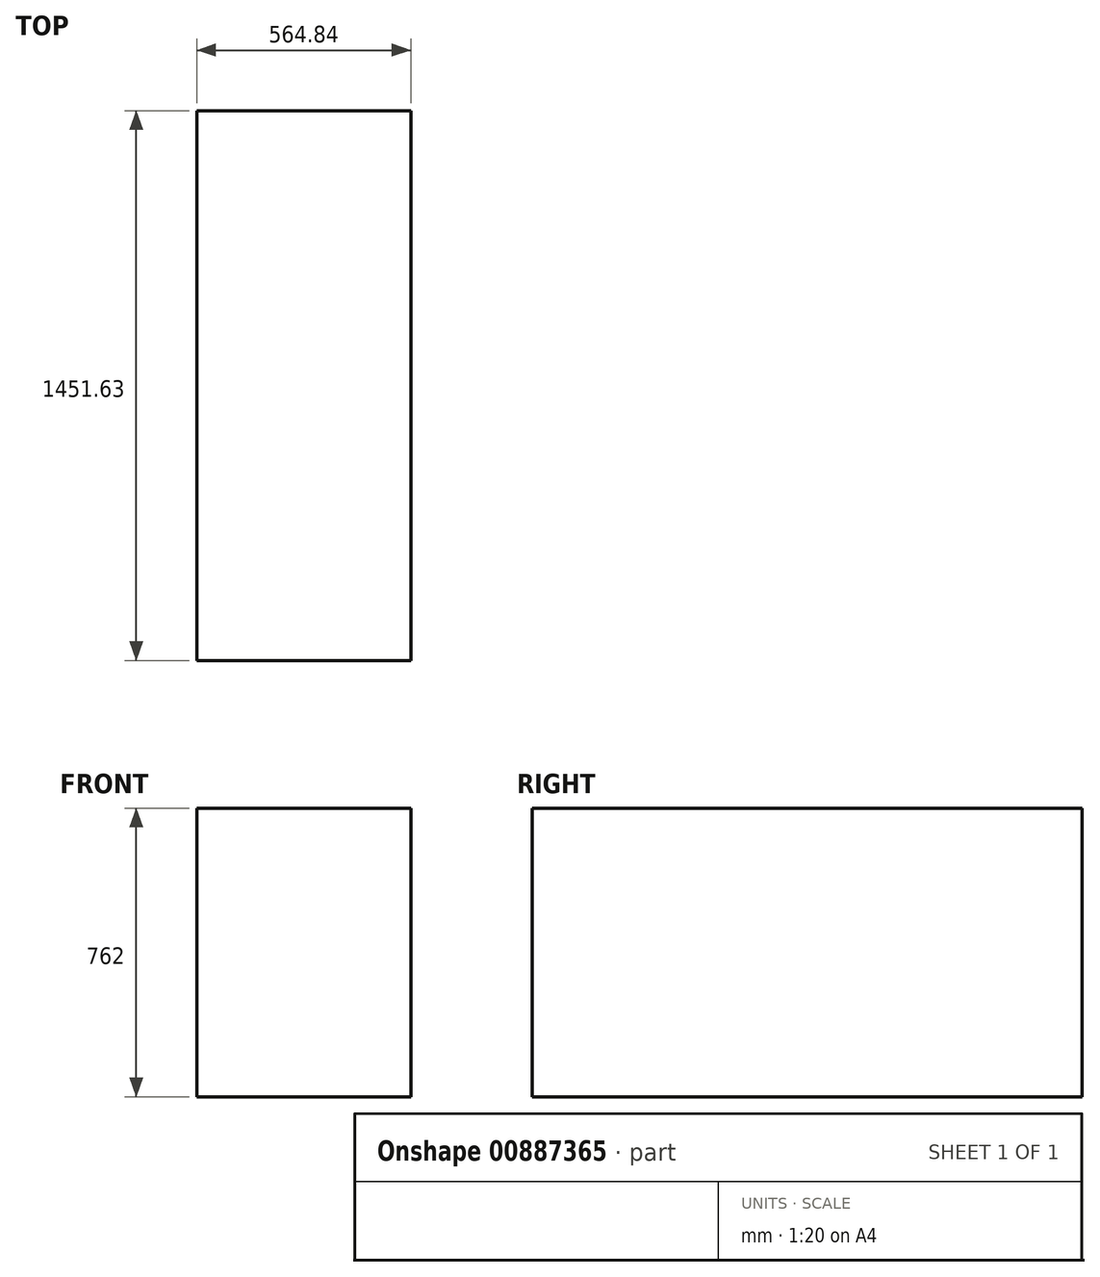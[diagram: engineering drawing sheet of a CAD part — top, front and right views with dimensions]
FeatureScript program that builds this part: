
annotation { "Feature Type Name" : "Feature", "Feature Type Description" : "" }
export const myFeature = defineFeature(function(context is Context, id is Id, definition is map)
    precondition{}
    {
        {
            var Q0;
            Q0=qCreatedBy(makeId("Top.planeOp"),FACE);
            var sketch = newSketch(context, id + "F0", { "sketchPlane" : qUnion([Q0])});
            skLineSegment(sketch, "E0.bottom", {"start": v(-170.22, 0) * mm, "end": v(4096.98, 0) * mm});
            skLineSegment(sketch, "E0.top", {"start": v(-170.22, -2082.8) * mm, "end": v(4096.98, -2082.8) * mm});
            skLineSegment(sketch, "E0.left", {"start": v(-170.22, 0) * mm, "end": v(-170.22, -2082.8) * mm});
            skLineSegment(sketch, "E0.right", {"start": v(4096.98, 0) * mm, "end": v(4096.98, -2082.8) * mm});
            skSolve(sketch);
        }
        {
            var Q0;
            Q0=makeQuery(id+"F0.imprint","IMPRINT",FACE,{"disambiguationData":[TD([[makeQuery(id+"F0.imprint","IMPRINT",EDGE,{"derivedFrom":sQuery(id+"F0.wireOp",EDGE,"E0.bottom")}),-1.0]])]});
            var sketch = newSketch(context, id + "F1", { "sketchPlane" : qUnion([Q0])});
            skLineSegment(sketch, "E1.bottom", {"start": v(-161.63, 0) * mm, "end": v(1209.97, 0) * mm});
            skLineSegment(sketch, "E1.top", {"start": v(-161.63, -1828.8) * mm, "end": v(1209.97, -1828.8) * mm});
            skLineSegment(sketch, "E1.left", {"start": v(-161.63, 0) * mm, "end": v(-161.63, -1828.8) * mm});
            skLineSegment(sketch, "E1.right", {"start": v(1209.97, 0) * mm, "end": v(1209.97, -1828.8) * mm});
            skSolve(sketch);
        }
        {
            var Q0;
            Q0=makeQuery(id+"F0.imprint","IMPRINT",FACE,{"disambiguationData":[TD([[makeQuery(id+"F0.imprint","IMPRINT",EDGE,{"derivedFrom":sQuery(id+"F0.wireOp",EDGE,"E0.bottom")}),-1.0]])]});
            var sketch = newSketch(context, id + "F2", { "sketchPlane" : qUnion([Q0])});
            skLineSegment(sketch, "E2.bottom", {"start": v(4091.6, -2083.31) * mm, "end": v(3526.75, -2083.31) * mm});
            skLineSegment(sketch, "E2.top", {"start": v(4091.6, -631.68) * mm, "end": v(3526.75, -631.68) * mm});
            skLineSegment(sketch, "E2.left", {"start": v(4091.6, -2083.31) * mm, "end": v(4091.6, -631.68) * mm});
            skLineSegment(sketch, "E2.right", {"start": v(3526.75, -2083.31) * mm, "end": v(3526.75, -631.68) * mm});
            skSolve(sketch);
        }
        {
            var Q0;
            Q0=makeQuery(id+"F1.imprint","IMPRINT",FACE,{"disambiguationData":[TD([[makeQuery(id+"F1.imprint","IMPRINT",EDGE,{"derivedFrom":sQuery(id+"F1.wireOp",EDGE,"E1.top")}),-1.0]])]});
            cPlane(context, id + "F3", {"entities" : qUnion([Q0]), "cplaneType" : CPlaneType.OFFSET, "offset" : 2438.4 * mm, "width" : 152.4 * mm, "height" : 152.4 * mm});
        }
        {
            var Q0;
            Q0=qCreatedBy(makeId("Right.planeOp"),FACE);
            cPlane(context, id + "F4", {"entities" : qUnion([Q0]), "cplaneType" : CPlaneType.OFFSET, "offset" : 1950.72 * mm, "width" : 152.4 * mm, "height" : 152.4 * mm});
        }
        {
            var Q0;
            Q0 = qSketchRegion(id + "F2", true);
            extrude(context, id + "F5", {"entities" : qUnion([Q0]), "depth" : 762 * mm, "offsetDistance" : 25.4 * mm});
        }
    });
